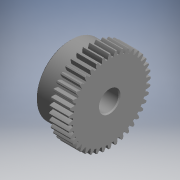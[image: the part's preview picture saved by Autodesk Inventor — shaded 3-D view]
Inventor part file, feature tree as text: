
AUTODESK INVENTOR PART (.ipt)
format: ipt  version: 2017.3 (Build 213256000, 256)  size: 467,968 bytes
history: native  units: mm (DEFAULTED — no unit token found)
features: sketch x2, revolve x1, extrude x1
ambient origin geometry x8: Origin, YZ Plane, XZ Plane, XY Plane, X Axis, Y Axis, Z Axis, Center Point
bodies: Solid1 (feature_tree)
feature tree (4):
  revolve  "Revolution1"  [1 undecoded]
  extrude  "Extrusion1"  [1 undecoded]
  sketch  "Sketch_8"  dims[d0=360.0deg d1=10.0mm d2=0.0mm]
  sketch  "Sketch_11"
note: 2 required parameter values undecoded (feature->parameter linkage not recoverable at this tier; creation-order binding heuristic only, values carry confidence <= 0.55)